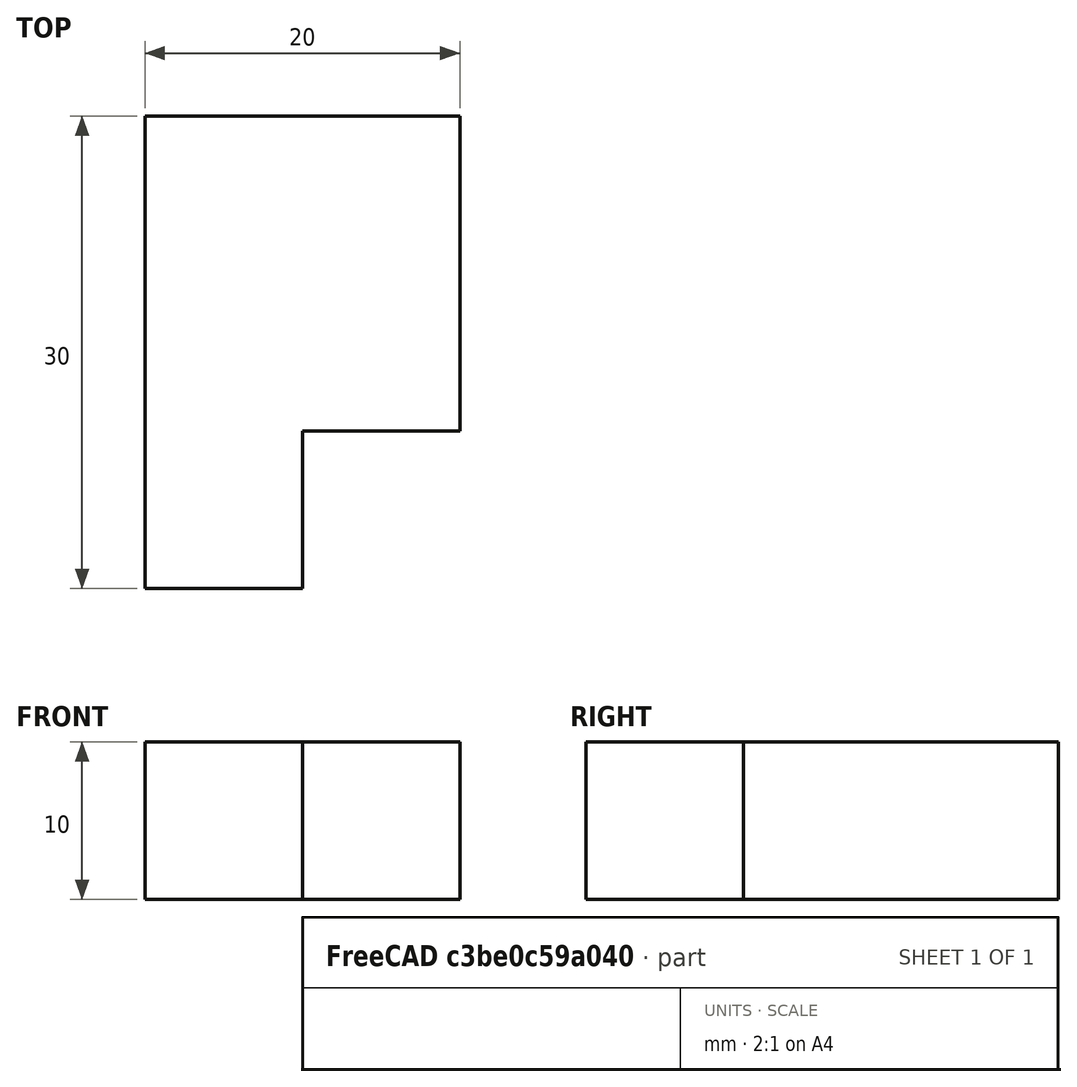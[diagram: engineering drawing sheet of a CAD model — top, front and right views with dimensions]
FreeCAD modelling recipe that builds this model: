
FCSTD DOCUMENT  (FreeCAD 0.16R)
Label: P
License: All rights reserved
LicenseURL: http://en.wikipedia.org/wiki/All_rights_reserved
objects: Sketcher::SketchObject×1, PartDesign::Pad×1
note: 3 computed .brp shape members not serialized (recipe doc carries the construction recipe); baked Part::Feature solids carry a one-line shape summary decoded from their .brp

FEATURE [Sketcher::SketchObject] Sketch
  sketch-geometry (6):
    g0: LineSegment StartX=-20 StartY=-10 StartZ=0 EndX=-20 EndY=20 EndZ=0
    g1: LineSegment StartX=-20 StartY=20 StartZ=0 EndX=0 EndY=20 EndZ=0
    g2: LineSegment StartX=0 StartY=20 StartZ=0 EndX=0 EndY=0 EndZ=0
    g3: LineSegment StartX=0 StartY=0 StartZ=0 EndX=-10 EndY=0 EndZ=0
    g4: LineSegment StartX=-10 StartY=0 StartZ=0 EndX=-10 EndY=-10 EndZ=0
    g5: LineSegment StartX=-10 StartY=-10 StartZ=0 EndX=-20 EndY=-10 EndZ=0
  constraints (18):
    c: Vertical(g0)
    c: Coincident(g0,g1)
    c: Horizontal(g1)
    c: Coincident(g1,g2)
    c: PointOnObject(g2,g-1)
    c: Coincident(g2,g3)
    c: Horizontal(g3)
    c: Coincident(g3,g4)
    c: Coincident(g4,g5)
    c: Distance(g1) = 20
    c: Distance(g2) = 20
    c: Perpendicular(g2,g1)
    c: Distance(g3) = 10
    c: Distance(g4) = 10
    c: Coincident(g5,g0)
    c: Perpendicular(g4,g5)
    c: Distance(g0) = 30
    c: Coincident(g2,g-1)
FEATURE [PartDesign::Pad] Pad
  Length = 10
  Length2 = 100
  Sketch = -> Sketch
  Type = 0
